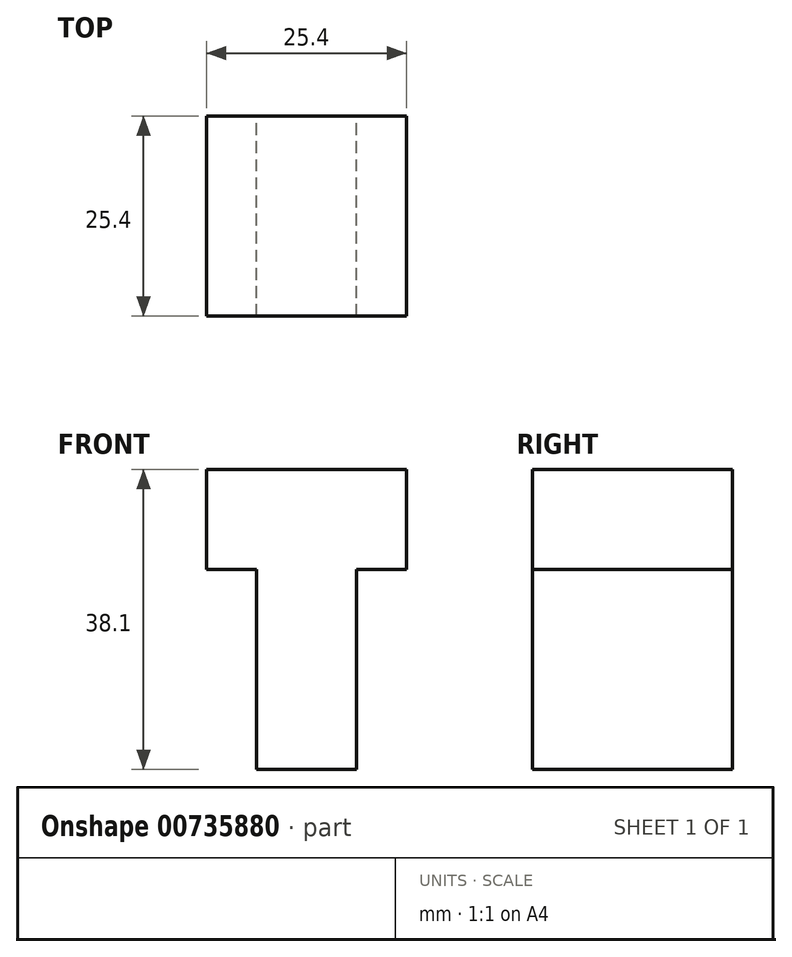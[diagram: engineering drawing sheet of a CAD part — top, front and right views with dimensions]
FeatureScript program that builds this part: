
annotation { "Feature Type Name" : "Feature", "Feature Type Description" : "" }
export const myFeature = defineFeature(function(context is Context, id is Id, definition is map)
    precondition{}
    {
        {
            var Q0;
            Q0=qCreatedBy(makeId("Front.planeOp"),FACE);
            var sketch = newSketch(context, id + "F0", { "sketchPlane" : qUnion([Q0])});
            skLineSegment(sketch, "E0", {"start": v(6.35, 0) * mm, "end": v(6.35, 25.4) * mm});
            skLineSegment(sketch, "E1", {"start": v(6.35, 25.4) * mm, "end": v(0, 25.4) * mm});
            skLineSegment(sketch, "E2", {"start": v(0, 25.4) * mm, "end": v(0, 38.1) * mm});
            skLineSegment(sketch, "E3", {"start": v(0, 38.1) * mm, "end": v(25.4, 38.1) * mm});
            skLineSegment(sketch, "E4", {"start": v(25.4, 38.1) * mm, "end": v(25.4, 25.4) * mm});
            skLineSegment(sketch, "E5", {"start": v(25.4, 25.4) * mm, "end": v(19.05, 25.4) * mm});
            skLineSegment(sketch, "E6", {"start": v(19.05, 25.4) * mm, "end": v(19.05, 0) * mm});
            skLineSegment(sketch, "E7", {"start": v(19.05, 0) * mm, "end": v(6.35, 0) * mm});
            skSolve(sketch);
        }
        {
            var Q0;
            Q0=makeQuery(id+"F0.imprint","IMPRINT",FACE,{"disambiguationData":[TD([[makeQuery(id+"F0.imprint","IMPRINT",EDGE,{"derivedFrom":sQuery(id+"F0.wireOp",EDGE,"E0")}),-1.0]])]});
            extrude(context, id + "F1", {"entities" : qUnion([Q0]), "depth" : 25.4 * mm, "offsetDistance" : 25.4 * mm});
        }
    });
